# Revit family: 0042930
name_source: partatom
category: Lighting Fixtures
units: mm (PartAtom-declared; Revit-internal decimal feet)

## family parameters
Cut with Voids When Loaded = No
Host = Face
Light Source = Yes
Maintain Annotation Orientation = No
OmniClass Number = 23.80.70.00
OmniClass Title = Lighting
Part Type = Normal
Room Calculation Point = No
Round Connector Dimension = Use Diameter
Shared = No

## types (1)
- DELTAWING 1200 4K
    Apparent Load = 39 VA
    Assembly Code = D5020200
    AssetType = Fixed
    ClassificationName = Uniclass2015
    ClassificationValue = EF_70_80
    Color Filter = 16777215
    Cost = 0 $
    Default Elevation = 1219 mm
    Description = DELTAWING 1200 4K is a ceiling and wall surface, suspended LED luminaire with opal diffuser, 1160x160x60mm dimensions, 35W system power, 4,600lm flux and 131lm/W efficacy, CRi (Ra) >80, 4000K (Neutral White) CCT, chromaticity tolerance of 3-step MacAdam ellipse, non-dimmable (4-steps DIP switch) driver (20W 2700lm, 25W 3350lm, 30W 4000lm, 35W 4600lm), RAL9003 finishing, L70B50 100khrs / L80B50 80khrs lifespan, IK06 impact resistance, IP44 ingress protection rating (in ceiling surface installation), Electrial protection Class I, Glow wire test 850°C.
    Dimming Lamp Color Temperature Shift = <None>
    DocumentationLiterature = https://www.sylvania-lighting.com code/0042930
    ElectricShockClassification = Class I
    EmergencyLight = No
    Emit Shape Visible in Rendering = No
    Emit from Rectangle Length = 1102 mm  [stored 3.61549 ft]
    Emit from Rectangle Width = 150 mm
    Export Type to IFC As = IfcLightFixtureType
    IfcExportAs = IfcLightFixtureType
    IfcExportType = IfcLightFixtureType
    ImpactProtectionIndex = IK06
    IngressProtection = IP44
    InputNominalFrequency = 50/60Hz
    InputVoltage = 220-240 V
    Keynote = 16500
    Lamp = LED
    LampColourRenderingIndex = 80
    LampColourTemperature = 4000 K
    LampMacAdamStep = 3
    LampNominalLuminous = 4600 lm
    LampsType = LED
    LuminaireType = Ceiling surface mounting,Wall surface mounted
    LuminousEfficacy = 131 lm/W
    Manufacturer = Feilo Sylvania
    ManufacturerName = Feilo Sylvania
    Material = PC Polycarbonate, Steel
    Material_1_SYL = Steel_RAL9003_White
    Material_2_SYL = Polycarbonate_RAL9003_White
    Material_3_SYL = Polycarbonate_Opal_4000K
    Material_4_SYL = <By Category>
    Model = DELTAWING 1200 4K
    ModelNumber = 0042930
    ModelReference = DELTAWING 1200 4K
    Name = DELTAWING 1200 4K
    NominalDepth = 160 mm
    NominalHeight = 60 mm
    NominalLength = 1160 mm
    Photometric Web File = 0042930.IES
    PowerConsumption = 35 W
    PowerFactor = 0.9
    Tilt Angle = -90.00°
    Type IFC Predefined Type = IfcLightFixtureType
    Type Image = <None>
    TypeName = Deltawing G2 1200
    URL = http://www.sylvania-group.com
    Voltage = 230 V
    WarrantyDescription = http://www.sylvania-group.com
    WarrantyDurationParts = 5
    WarrantyDurationUnit = Years
    Weight = 1.965 kg

note: [stored X ft] marks values corroborated as IEEE doubles in the binary element streams (Revit-internal decimal feet)

## geometry (parser evidence)
native form markers: Sweep x3
no freeform markers — native parametric forms only
